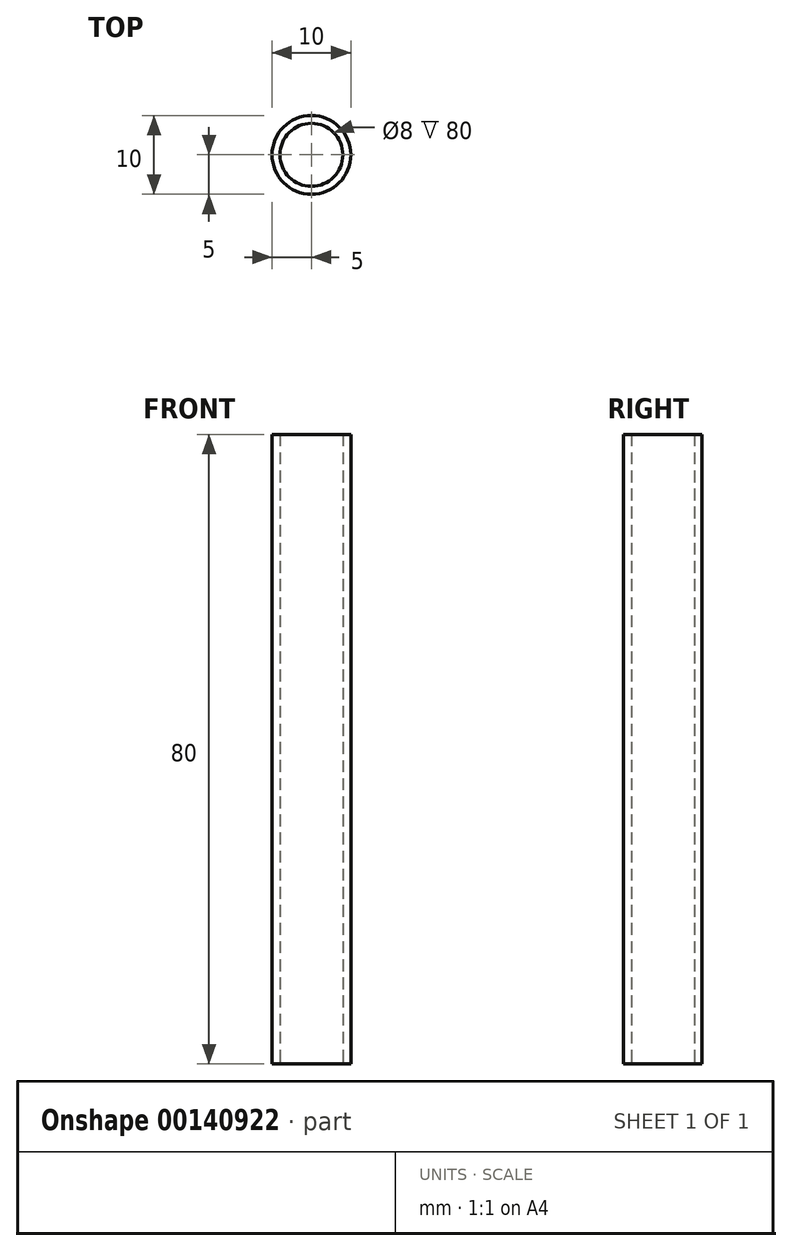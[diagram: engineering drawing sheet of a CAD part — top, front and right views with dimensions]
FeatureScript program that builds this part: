
annotation { "Feature Type Name" : "Feature", "Feature Type Description" : "" }
export const myFeature = defineFeature(function(context is Context, id is Id, definition is map)
    precondition{}
    {
        {
            var Q0;
            Q0=qCreatedBy(makeId("Top.planeOp"),FACE);
            var sketch = newSketch(context, id + "F0", { "sketchPlane" : qUnion([Q0])});
            skCircle(sketch, "E0", {"center": v(0, 0) * mm, "radius": 5 * mm});
            skCircle(sketch, "E1", {"center": v(0, 0) * mm, "radius": 4 * mm});
            skSolve(sketch);
        }
        {
            var Q0;
            Q0=makeQuery(id+"F0.imprint","IMPRINT",FACE,{"disambiguationData":[TD([[makeQuery(id+"F0.imprint","IMPRINT",EDGE,{"derivedFrom":sQuery(id+"F0.wireOp",EDGE,"E0")}),1.0]])]});
            extrude(context, id + "F1", {"entities" : qUnion([Q0]), "depth" : 80 * mm});
        }
    });
